# Revit family: Urinal-Wall_Mount-KOHLER-Tend-K-28081T_1
name_source: partatom
category: Plumbing Fixtures
units: mm (PartAtom-declared; Revit-internal decimal feet)

## family parameters
Cut with Voids When Loaded = No
Host = Face
OmniClass Number = 23.31.21.00
OmniClass Title = Urinals
Part Type = Normal
Room Calculation Point = No
Round Connector Dimension = Use Diameter
Shared = No

## types (2) — shared parameters
ADA Compliant = No
Assembly Code = D2010200
CW Connection = Yes
Cold Water Inlet = Cold Water Inlet
Date Modified = 08/29/2022
Default Elevation = 0"
Drain Included = No
Finish = Kohler-Vitreous_China-0-White
Flow Rate = 0 GPM
HW Connection = No
Height = 21 15/16"
Hot Water Inlet = Hot Water Inlet
Length = 14 13/16"
Manufacturer = Kohler Co.
Master Format 2014 = 22 41 13.16
Master Format 2014 Name = Residential Urinals
Material = Vitreous China
Pressure = 0.00 psi
Product Name = Tend
URL = http://www.kohler.com.cn
Vent Connection = No
Waste Connection = Yes
Waste Water Outlet = Waste Water Outlet
WaterSense Certified = No
Width = 13 1/16"

## per-type parameters (varying)
| type | Description | Flush Rate- GPF | Flush Rate- LPF | Model | Type |
| 2.5L, Touchless, 0-White | WH TOUCHLESS URINAL 2.5L | 0.66 GPF | 2.5 LPF | K-28081T-0 | 1 |
| 0.5L, Eco Touchless, 0-White | WH ECO TOUCHLESS URINAL 0.5L | 0.13 GPF | 0.5 LPF | K-28081T-Y-0 | 2 |

## geometry (parser evidence)
native form markers: Sweep x4
no freeform markers — native parametric forms only
